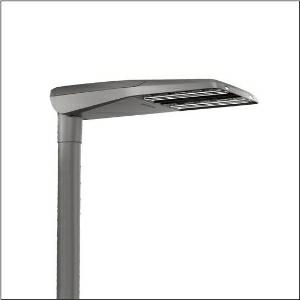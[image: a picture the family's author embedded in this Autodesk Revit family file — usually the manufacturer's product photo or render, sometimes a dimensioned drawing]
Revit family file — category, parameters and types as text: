
# Revit family: streetlight_sl_11_iq_midi___st1_0ab_5xc3n51f08le_f358
name_source: partatom
category: Lighting Fixtures
units: mm (PartAtom-declared; Revit-internal decimal feet)

## family parameters
Cut with Voids When Loaded = No
Host = Face
Light Source = No
Part Type = Normal
Room Calculation Point = No
Round Connector Dimension = Use Diameter
Shared = No

## types (1)
- --- (1 x LED, 7760 lm, 60.4 W, 3000K)
    Apparent Load = 60 VA
    CIE Flux Codes = 29 63 95 100 100
    Color Rendering = 70
    Color Temperature = 3000K
    Default Elevation = 1800 mm
    Description = Streetlight SL 11 iQ midi, mast luminaire, primary light control with 3 zone facetted reflector, of plastic, silver coated, highly specular, primary optical cover: cover, of PMMA, transparent, light distribution: ST1.0aB, light emission: direct distribution, primary light characteristic: asymmetric, installation type: post-top, side-entry, lamps: LED, High Power LED, rated values: 7.760lm | 60,4W | 128,5lm/W (begin service life); end service life: 7.760lm | 62,5W; at 50% lumin. flux: 3.880lm | 29,6W | 131,1lm/W, colour temperature: 3000K, colour rendering: CRI > 70, light colour: 730, light setting 1 begin service life: 100% | 7.760lm | 60,4W | 128,5lm/W | 3.000K, light setting 1 end service life: 62,5W, further light settings possible, control: optimised constant luminous flux control (CLO 2.0), Street-Remote, Desk-Remote (wireless, voltage-free reading and setting of iQ features in the workshop via application-optimized NFC function/RFID function), Light-Fading, Smart-Wire, Night-Set, Lumen-Switch, Temp-Guard, Auto-Match, with cable H07RN-F 3x 1.5mm², mains connection: 230..240V, AC, 50/60Hz, connection cable pre-assembled, cable length: 8,5m, luminaire housing, of diecast aluminium, powder-coated, SITECO metallic grey (DB 702S), please order mast flange separately, inclination adjustable without tools: 0°, 5°, 10°, 15° (post-top) | 0°, -5°, -10°, -15° (side-entry), sealing non-destructively replaceable, multi-level sealing system, length: 780mm, width: 376mm, height: 118mm, mast flange for spigot size: 42mm (side-entry): 5XC10008XM4, 60/48mm (side-entry/post-top): 5XC10108XM2, 76/60mm (side-entry/post-top): 5XC10108XM1, equipment: standard, protection rating (complete): IP66, insulation class (complete): insulation class II (safety insulation), certification: CE, ENEC, ENEC+, VDE, impact resistance: IK10, permissible operating ambient temperature for outdoor applications: -25..+50°C, standard-compliant lighting for roads and squares, Environmental Product Declaration (EPD) tested and certified by an independent institute, packaging unit: 1 piece

Light Distribution: ST1.0aB
    Height = 118 mm
    Lamp = 1 x LED
    Lamp Light Flux = 7760 lm
    Lamp Power = 60.4 W
    Lamp count = 1
    Length = 780 mm
    Luminous efficacy = 128 lm/W
    Manufacturer = Siteco
    ModVariant = No
    Model = 5XC3N51F08LE
    Number of Poles = 1
    OnlyDefault = Yes
    Power Factor = 1
    Product Name = Streetlight SL 11 iQ midi | ST1.0aB
    Product group = mast luminaire | pylon top
    ProductGroupID = 6100
    Protection Class = Protection class II
    Protection Degree = IP 66
    RLX_Detail_Level = 1
    RLX_Emergency_Light_Flux = 0 lm
    RLX_Emergency_Type = 0
    RLX_Emergency_Type_DB = No
    RlxData = <blob elided: 70277 chars, md5=ec02ea77>
    Socket = socket
    Standby Power = 0 W
    System Light Flux = 7760 lm
    System Power = 60 W
    Type Comments = factory setting: luminous flux: 100 % | dim-lin: 254 | 520 mA
    Type Image = l_1005960.jpg
    URL = http://relux.com
    VarID = @adj_091819
    Voltage = 0 V
    Weight = 0.00 kg
    Width = 376 mm

## geometry (parser evidence)
native form markers: Blend x4, Sweep x10
no freeform markers — native parametric forms only
